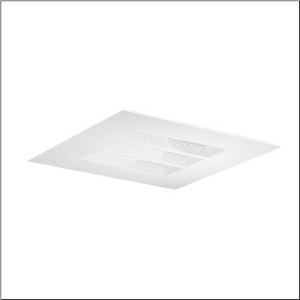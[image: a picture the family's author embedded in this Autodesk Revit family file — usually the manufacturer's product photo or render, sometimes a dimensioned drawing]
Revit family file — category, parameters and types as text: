
# Revit family: taris_r__21_51mt1ld0jhfedc02_d728
name_source: partatom
category: Lighting Fixtures
units: mm (PartAtom-declared; Revit-internal decimal feet)

## family parameters
Cut with Voids When Loaded = No
Host = Face
Light Source = No
Part Type = Normal
Room Calculation Point = No
Round Connector Dimension = Use Diameter
Shared = No

## types (1)
- --- (1 x LED, 4290 lm, 27.4 W, 3000K)
    Apparent Load = 27 VA
    CIE Flux Codes = 79 97 100 100 100
    Color Rendering = 80
    Color Temperature = 3000K
    Default Elevation = 1800 mm
    Description = Taris® 21, office luminaire, primary anti-glare with micro louvre, primary optical cover: axial lens, of PMMA, structured, CAT 2 (L<= 1500cd/m²), light emission: direct distribution, primary light characteristic: symmetric, installation type: lay-in mounting, LED rated luminous flux: 4.290 lm, light colour: 830, colour temperature: 3000K, control gear: ECG DALI, with terminal, 5-pole, mains connection: 230V, AC, 50Hz, rated input power: 27W, housing, luminaire housing, of plastic, traffic white (RAL 9016), module: M600, length: 597 mm, width: 597 mm, height: 42mm, protection rating (complete): IP20, insulation class (complete): insulation class I (protective earthing), certification: CE, ENEC, VDE, protection symbol: F, impact resistance: IK02, permissible ambient temperature for indoor applications: 0..+35°C, standard: EN 50419, packaging unit: 1 piece
    Height = 0 mm  [stored 0 ft]
    Lamp = 1 x LED
    Lamp Light Flux = 4290 lm
    Lamp Power = 27.4 W
    Lamp count = 1
    Length = 597 mm
    Luminous efficacy = 157 lm/W
    Manufacturer = Siteco
    ModVariant = No
    Model = 51MT1LD0JHFEDC02
    Mounting Place = Ceiling
    Mounting Type = Recessed
    Number of Poles = 1
    OnlyDefault = Yes
    Power Factor = 1
    Product Name = Taris® 21
    Product group = office luminaire | ceiling recessed
    ProductGroupID = 400
    Protection Class = Protection class I
    Protection Degree = IP 20
    RLX_Detail_Level = 1
    RlxData = <blob elided: 23173 chars, md5=dc66260b>
    Socket = socket
    Standby Power = 0 W
    System Light Flux = 4290 lm
    System Power = 27 W
    Type Comments = factory setting: luminous flux: 100 % | dim-lin: 254 | 250 mA
    Type Image = l_1004820.jpg
    URL = http://relux.com
    VarID = @adj_130491
    Voltage = 0 V
    Weight = 0.00 kg
    Width = 597 mm

note: [stored X ft] marks values corroborated as IEEE doubles in the binary element streams (Revit-internal decimal feet)

## geometry (parser evidence)
native form markers: Blend x4, Sweep x11
no freeform markers — native parametric forms only
